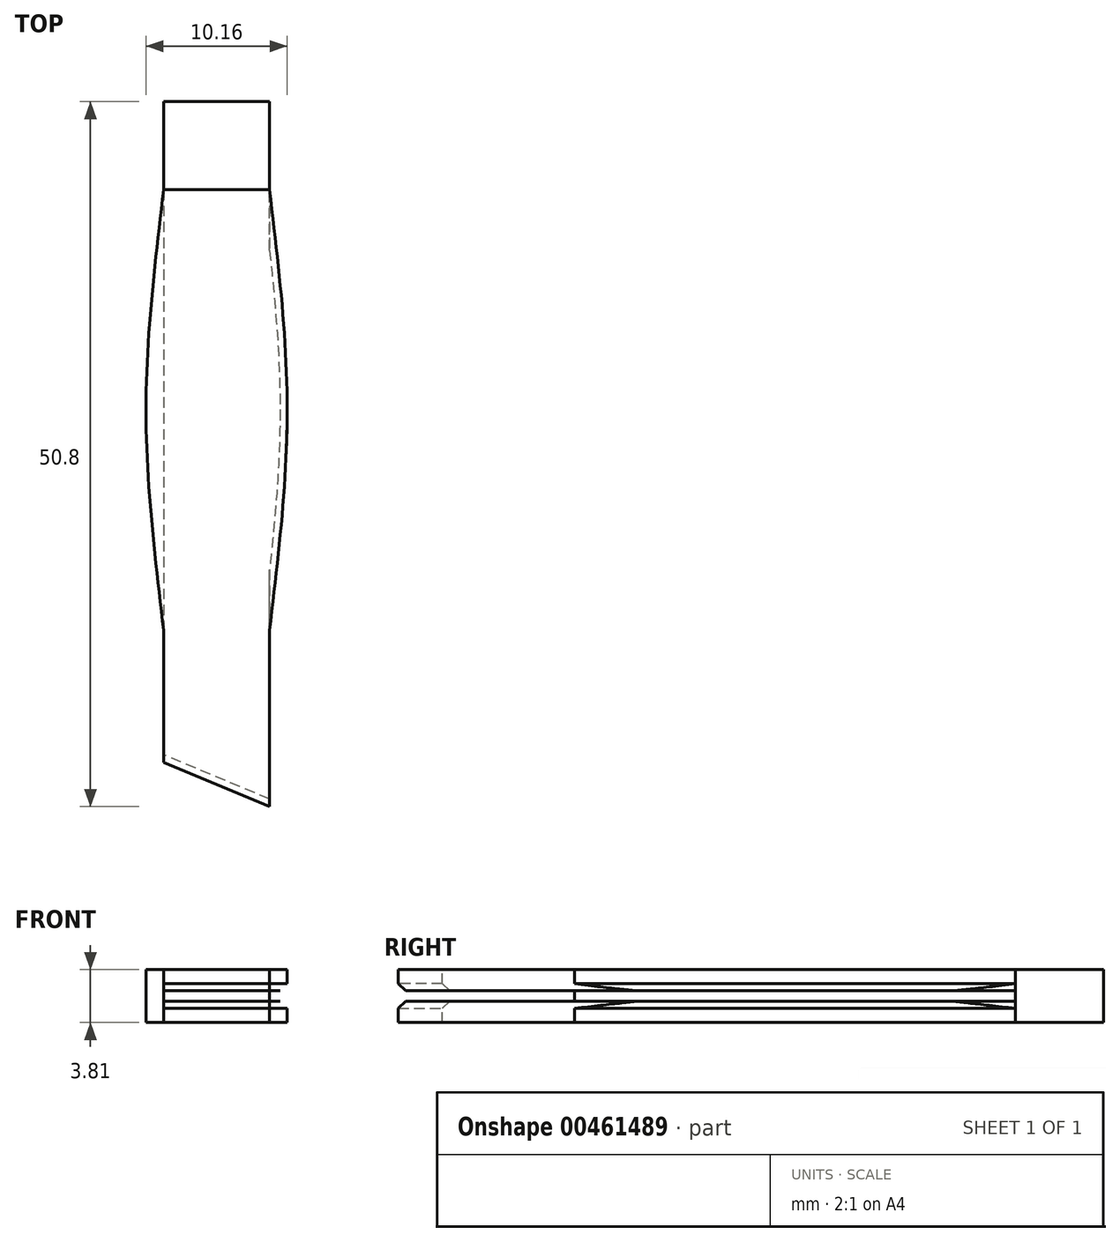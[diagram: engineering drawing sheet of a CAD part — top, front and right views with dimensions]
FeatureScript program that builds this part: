
annotation { "Feature Type Name" : "Feature", "Feature Type Description" : "" }
export const myFeature = defineFeature(function(context is Context, id is Id, definition is map)
    precondition{}
    {
        {
            var Q0;
            Q0=qCreatedBy(makeId("Front.planeOp"),FACE);
            var sketch = newSketch(context, id + "F0", { "sketchPlane" : qUnion([Q0])});
            skLineSegment(sketch, "E0.bottom", {"start": v(0, 0) * mm, "end": v(7.62, 0) * mm});
            skLineSegment(sketch, "E0.top", {"start": v(0, 3.81) * mm, "end": v(7.62, 3.81) * mm});
            skLineSegment(sketch, "E0.left", {"start": v(0, 0) * mm, "end": v(0, 3.81) * mm});
            skLineSegment(sketch, "E0.right", {"start": v(7.62, 0) * mm, "end": v(7.62, 3.81) * mm});
            skSolve(sketch);
        }
        {
            var Q0;
            Q0=makeQuery(id+"F0.imprint","IMPRINT",FACE,{"disambiguationData":[TD([[makeQuery(id+"F0.imprint","IMPRINT",EDGE,{"derivedFrom":sQuery(id+"F0.wireOp",EDGE,"E0.bottom")}),1.0]])]});
            extrude(context, id + "F1", {"entities" : qUnion([Q0]), "depth" : 6.35 * mm});
        }
        {
            var Q0;
            Q0=qCreatedBy(makeId("Top.planeOp"),FACE);
            var sketch = newSketch(context, id + "F2", { "sketchPlane" : qUnion([Q0])});
            skLineSegment(sketch, "E1.bottom", {"start": v(0, 0) * mm, "end": v(7.62, 0) * mm});
            skLineSegment(sketch, "E1.top", {"start": v(0, -6.35) * mm, "end": v(7.62, -6.35) * mm});
            skLineSegment(sketch, "E1.left", {"start": v(0, 0) * mm, "end": v(0, -6.35) * mm});
            skLineSegment(sketch, "E1.right", {"start": v(7.62, 0) * mm, "end": v(7.62, -6.35) * mm});
            skLineSegment(sketch, "E2", {"start": v(0, -6.35) * mm, "end": v(0, -12.7) * mm});
            skLineSegment(sketch, "E3", {"start": v(7.62, -6.35) * mm, "end": v(7.62, -12.7) * mm});
            skLineSegment(sketch, "E4", {"start": v(0, -44.45) * mm, "end": v(7.62, -44.45) * mm});
            skLineSegment(sketch, "E5.top", {"start": v(0, -57.15) * mm, "end": v(7.62, -57.15) * mm});
            skLineSegment(sketch, "E5.left", {"start": v(0, -44.45) * mm, "end": v(0, -57.15) * mm});
            skLineSegment(sketch, "E5.right", {"start": v(7.62, -44.45) * mm, "end": v(7.62, -57.15) * mm});
            skLineSegment(sketch, "E6", {"start": v(0, -12.7) * mm, "end": v(0, -44.45) * mm});
            skLineSegment(sketch, "E7", {"start": v(7.62, -12.7) * mm, "end": v(7.62, -44.45) * mm});
            skLineSegment(sketch, "E8", {"start": v(7.62, -28.58) * mm, "end": v(0, -28.58) * mm});
            skLineSegment(sketch, "E9", {"start": v(0, -28.58) * mm, "end": v(-1.27, -28.58) * mm});
            skLineSegment(sketch, "E10", {"start": v(7.62, -28.58) * mm, "end": v(8.9, -28.58) * mm});
            skFitSpline(sketch, "E11", {"points": [v(0, -12.7) * mm, v(-1.27, -28.58) * mm, v(0, -44.45) * mm], "startDerivative": vector(-3.81, -31.75) * mm, "endDerivative": vector(3.81, -31.75) * mm});
            skFitSpline(sketch, "E12", {"points": [v(7.62, -12.7) * mm, v(8.9, -28.58) * mm, v(7.62, -44.45) * mm], "startDerivative": vector(3.81, -31.75) * mm, "endDerivative": vector(-3.81, -31.75) * mm});
            skSolve(sketch);
        }
        {
            var Q0;
            Q0=makeQuery(id+"F2.imprint","IMPRINT",FACE,{"disambiguationData":[TD([[makeQuery(id+"F2.imprint","IMPRINT",EDGE,{"derivedFrom":sQuery(id+"F2.wireOp",EDGE,"E1.top")}),-1.0]])]});
            var Q1;
            Q1=makeQuery(id+"F2.imprint","IMPRINT",FACE,{"disambiguationData":[TD([[makeQuery(id+"F2.imprint","IMPRINT",EDGE,{"derivedFrom":sQuery(id+"F2.wireOp",EDGE,"E5.top")}),1.0]])]});
            var Q2;
            {var subQ3=sQuery(id+"F2.wireOp",EDGE,"E9");Q2=makeQuery(id+"F2.imprint","IMPRINT",FACE,{"disambiguationData":[TD([[makeQuery(id+"F2.imprint","IMPRINT",EDGE,{"derivedFrom":subQ3}),1.0]])]});}
            var Q3;
            {var subQ3=sQuery(id+"F2.wireOp",EDGE,"E9");Q3=makeQuery(id+"F2.imprint","IMPRINT",FACE,{"disambiguationData":[TD([[makeQuery(id+"F2.imprint","IMPRINT",EDGE,{"derivedFrom":subQ3}),-1.0]])]});}
            var Q4;
            {var subQ3=sQuery(id+"F2.wireOp",EDGE,"E8");Q4=makeQuery(id+"F2.imprint","IMPRINT",FACE,{"disambiguationData":[TD([[makeQuery(id+"F2.imprint","IMPRINT",EDGE,{"derivedFrom":subQ3}),1.0]])]});}
            var Q5;
            {var subQ3=sQuery(id+"F2.wireOp",EDGE,"E10");Q5=makeQuery(id+"F2.imprint","IMPRINT",FACE,{"disambiguationData":[TD([[makeQuery(id+"F2.imprint","IMPRINT",EDGE,{"derivedFrom":subQ3}),-1.0]])]});}
            var Q6;
            {var subQ3=sQuery(id+"F2.wireOp",EDGE,"E10");Q6=makeQuery(id+"F2.imprint","IMPRINT",FACE,{"disambiguationData":[TD([[makeQuery(id+"F2.imprint","IMPRINT",EDGE,{"derivedFrom":subQ3}),1.0]])]});}
            extrude(context, id + "F3", {"entities" : qUnion([Q0, Q1, Q2, Q3, Q4, Q5, Q6]), "operationType" : NewBodyOperationType.ADD, "depth" : 3.8 * mm});
        }
        {
            var Q0;
            Q0=makeQuery(id+"F3.opExtrude","SWEPT_FACE",FACE,{"disambiguationData":[OSD([sQuery(id+"F2.wireOp",EDGE,"E5.top")])]});
            var sketch = newSketch(context, id + "F4", { "sketchPlane" : qUnion([Q0])});
            skLineSegment(sketch, "E13", {"start": v(0, 3.81) * mm, "end": v(7.62, 3.81) * mm});
            skLineSegment(sketch, "E14.bottom", {"start": v(-4.88, 3.81) * mm, "end": v(12.52, 3.81) * mm});
            skLineSegment(sketch, "E14.top", {"start": v(-4.88, 0) * mm, "end": v(12.52, 0) * mm});
            skLineSegment(sketch, "E14.left", {"start": v(-4.88, 3.81) * mm, "end": v(-4.88, 0) * mm});
            skLineSegment(sketch, "E15", {"start": v(-4.88, 3.81) * mm, "end": v(-4.88, 2.29) * mm});
            skLineSegment(sketch, "E16", {"start": v(-4.88, 0) * mm, "end": v(-4.88, 1.52) * mm});
            skLineSegment(sketch, "E17", {"start": v(12.52, 0) * mm, "end": v(12.52, 1.52) * mm});
            skLineSegment(sketch, "E18.bottom", {"start": v(-4.88, 2.29) * mm, "end": v(12.52, 2.29) * mm});
            skLineSegment(sketch, "E18.top", {"start": v(-4.88, 1.52) * mm, "end": v(12.52, 1.52) * mm});
            skLineSegment(sketch, "E18.left", {"start": v(-4.88, 2.29) * mm, "end": v(-4.88, 1.52) * mm});
            skLineSegment(sketch, "E18.right", {"start": v(12.52, 2.29) * mm, "end": v(12.52, 1.52) * mm});
            skSolve(sketch);
        }
        {
            var Q0;
            {var subQ0=sQuery(id+"F4.wireOp",EDGE,"E18.bottom");var subQ1=sQuery(id+"F2.wireOp",EDGE,"E5.top");var subQ2=makeQuery(id+"F3.opExtrude","SWEPT_EDGE",EDGE,{"disambiguationData":[OSD([subQ1,sQuery(id+"F2.wireOp",EDGE,"E5.right")])]});var subQ3=makeQuery(id+"F4.imprint","INTERSECT",VERTEX,{"derivedFrom":[subQ2,subQ0]});Q0=makeQuery(id+"F4.imprint","IMPRINT",FACE,{"disambiguationData":[TD([[makeQuery(id+"F4.imprint","IMPRINT",EDGE,{"disambiguationData":[TD([[subQ3,1.0]])],"derivedFrom":subQ0}),-1.0]])]});}
            var Q1;
            {var subQ0=sQuery(id+"F4.wireOp",EDGE,"E18.left");Q1=makeQuery(id+"F4.imprint","IMPRINT",FACE,{"disambiguationData":[TD([[makeQuery(id+"F4.imprint","IMPRINT",EDGE,{"derivedFrom":subQ0}),1.0]])]});}
            var Q2;
            {var subQ0=sQuery(id+"F4.wireOp",EDGE,"E18.right");Q2=makeQuery(id+"F4.imprint","IMPRINT",FACE,{"disambiguationData":[TD([[makeQuery(id+"F4.imprint","IMPRINT",EDGE,{"derivedFrom":subQ0}),-1.0]])]});}
            extrude(context, id + "F5", {"entities" : qUnion([Q0, Q1, Q2]), "operationType" : NewBodyOperationType.REMOVE, "oppositeDirection" : true, "depth" : 50.8 * mm});
        }
        {
            var Q0;
            Q0=makeQuery(id+"F3.boolean.opBoolean","MERGE",FACE,{"derivedFrom":[makeQuery(id+"F1.opExtrude","SWEPT_FACE",FACE,{"disambiguationData":[OSD([sQuery(id+"F0.wireOp",EDGE,"E0.top")])]}),makeQuery(id+"F3.opExtrude","CAP_FACE",FACE,{"disambiguationData":[OSD([sQuery(id+"F2.wireOp",EDGE,"E1.top"),sQuery(id+"F2.wireOp",EDGE,"E2"),sQuery(id+"F2.wireOp",EDGE,"E3"),sQuery(id+"F2.wireOp",EDGE,"277f9b0c-e394-4d01-b2aa-9fb8e24fa29d"),sQuery(id+"F2.wireOp",EDGE,"5b10a53d-1cbc-4650-926f-43f652588418"),sQuery(id+"F2.wireOp",EDGE,"E4"),sQuery(id+"F2.wireOp",EDGE,"E5.top"),sQuery(id+"F2.wireOp",EDGE,"E5.left"),sQuery(id+"F2.wireOp",EDGE,"E5.right")])],"isStart":false})]});
            var sketch = newSketch(context, id + "F6", { "sketchPlane" : qUnion([Q0])});
            skLineSegment(sketch, "E19", {"start": v(0, -44.45) * mm, "end": v(7.62, -44.45) * mm});
            skLineSegment(sketch, "E20.top", {"start": v(0, -57.15) * mm, "end": v(7.62, -57.15) * mm});
            skLineSegment(sketch, "E20.left", {"start": v(0, -44.45) * mm, "end": v(0, -57.15) * mm});
            skLineSegment(sketch, "E20.right", {"start": v(7.62, -44.45) * mm, "end": v(7.62, -57.15) * mm});
            skLineSegment(sketch, "E21", {"start": v(7.62, -57.15) * mm, "end": v(0, -53.98) * mm});
            skSolve(sketch);
        }
        {
            var Q0;
            {var subQ0=sQuery(id+"F6.wireOp",EDGE,"E20.top");Q0=makeQuery(id+"F6.imprint","IMPRINT",FACE,{"disambiguationData":[TD([[makeQuery(id+"F6.imprint","IMPRINT",EDGE,{"derivedFrom":subQ0}),1.0]])]});}
            extrude(context, id + "F7", {"entities" : qUnion([Q0]), "operationType" : NewBodyOperationType.REMOVE, "oppositeDirection" : true, "depth" : 25.4 * mm});
        }
        {
            var Q0;
            Q0=makeQuery(id+"F7.boolean.opBoolean","INTERSECT",EDGE,{"derivedFrom":[makeQuery(id+"F5.boolean.opBoolean","COPY",FACE,{"derivedFrom":makeQuery(id+"F5.opExtrude","SWEPT_FACE",FACE,{"disambiguationData":[OSD([sQuery(id+"F4.wireOp",EDGE,"E18.bottom")])]})}),makeQuery(id+"F7.opExtrude","SWEPT_FACE",FACE,{"disambiguationData":[OSD([sQuery(id+"F6.wireOp",EDGE,"E21")])]})]});
            var Q1;
            Q1=makeQuery(id+"F7.boolean.opBoolean","INTERSECT",EDGE,{"derivedFrom":[makeQuery(id+"F5.boolean.opBoolean","COPY",FACE,{"derivedFrom":makeQuery(id+"F5.opExtrude","SWEPT_FACE",FACE,{"disambiguationData":[OSD([sQuery(id+"F4.wireOp",EDGE,"E18.top")])]})}),makeQuery(id+"F7.opExtrude","SWEPT_FACE",FACE,{"disambiguationData":[OSD([sQuery(id+"F6.wireOp",EDGE,"E21")])]})]});
            var Q2;
            Q2=makeQuery(id+"F5.boolean.opBoolean","INTERSECT",EDGE,{"derivedFrom":[makeQuery(id+"F3.opExtrude","SWEPT_FACE",FACE,{"disambiguationData":[OSD([sQuery(id+"F2.wireOp",EDGE,"E11")])]}),makeQuery(id+"F5.opExtrude","SWEPT_FACE",FACE,{"disambiguationData":[OSD([sQuery(id+"F4.wireOp",EDGE,"E18.bottom")])]})]});
            var Q3;
            Q3=makeQuery(id+"F5.boolean.opBoolean","INTERSECT",EDGE,{"derivedFrom":[makeQuery(id+"F3.opExtrude","SWEPT_FACE",FACE,{"disambiguationData":[OSD([sQuery(id+"F2.wireOp",EDGE,"E12")])]}),makeQuery(id+"F5.opExtrude","SWEPT_FACE",FACE,{"disambiguationData":[OSD([sQuery(id+"F4.wireOp",EDGE,"E18.bottom")])]})]});
            var Q4;
            Q4=makeQuery(id+"F5.boolean.opBoolean","INTERSECT",EDGE,{"derivedFrom":[makeQuery(id+"F3.opExtrude","SWEPT_FACE",FACE,{"disambiguationData":[OSD([sQuery(id+"F2.wireOp",EDGE,"E12")])]}),makeQuery(id+"F5.opExtrude","SWEPT_FACE",FACE,{"disambiguationData":[OSD([sQuery(id+"F4.wireOp",EDGE,"E18.top")])]})]});
            var Q5;
            Q5=makeQuery(id+"F5.boolean.opBoolean","INTERSECT",EDGE,{"derivedFrom":[makeQuery(id+"F3.opExtrude","SWEPT_FACE",FACE,{"disambiguationData":[OSD([sQuery(id+"F2.wireOp",EDGE,"E11")])]}),makeQuery(id+"F5.opExtrude","SWEPT_FACE",FACE,{"disambiguationData":[OSD([sQuery(id+"F4.wireOp",EDGE,"E18.top")])]})]});
            chamfer(context, id + "F8", {"entities" : qUnion([Q0, Q1, Q2, Q3, Q4, Q5]), "width" : 0.5 * mm, "tangentPropagation" : true});
        }
        {
            var Q0;
            Q0=makeQuery(id+"F3.boolean.opBoolean","MERGE",FACE,{"derivedFrom":[makeQuery(id+"F1.opExtrude","SWEPT_FACE",FACE,{"disambiguationData":[OSD([sQuery(id+"F0.wireOp",EDGE,"E0.top")])]}),makeQuery(id+"F3.opExtrude","CAP_FACE",FACE,{"disambiguationData":[OSD([sQuery(id+"F2.wireOp",EDGE,"E1.top"),sQuery(id+"F2.wireOp",EDGE,"E2"),sQuery(id+"F2.wireOp",EDGE,"E3"),sQuery(id+"F2.wireOp",EDGE,"E5.top"),sQuery(id+"F2.wireOp",EDGE,"E5.left"),sQuery(id+"F2.wireOp",EDGE,"E5.right"),sQuery(id+"F2.wireOp",EDGE,"E11"),sQuery(id+"F2.wireOp",EDGE,"E12")])],"isStart":false})]});
            var sketch = newSketch(context, id + "F9", { "sketchPlane" : qUnion([Q0])});
            skLineSegment(sketch, "E22.bottom", {"start": v(0, 0) * mm, "end": v(7.62, 0) * mm});
            skLineSegment(sketch, "E22.top", {"start": v(0, -12.7) * mm, "end": v(7.62, -12.7) * mm});
            skLineSegment(sketch, "E22.left", {"start": v(0, 0) * mm, "end": v(0, -12.7) * mm});
            skLineSegment(sketch, "E22.right", {"start": v(7.62, 0) * mm, "end": v(7.62, -12.7) * mm});
            skSolve(sketch);
        }
        {
            var Q0;
            Q0=makeQuery(id+"F9.imprint","IMPRINT",FACE,{"disambiguationData":[TD([[makeQuery(id+"F9.imprint","IMPRINT",EDGE,{"derivedFrom":sQuery(id+"F9.wireOp",EDGE,"E22.bottom")}),-1.0]])]});
            extrude(context, id + "F10", {"entities" : qUnion([Q0]), "operationType" : NewBodyOperationType.REMOVE, "oppositeDirection" : true, "depth" : 25.4 * mm});
        }
        {
            var Q0;
            Q0=makeQuery(id+"F3.boolean.opBoolean","MERGE",FACE,{"derivedFrom":[makeQuery(id+"F1.opExtrude","SWEPT_FACE",FACE,{"disambiguationData":[OSD([sQuery(id+"F0.wireOp",EDGE,"E0.top")])]}),makeQuery(id+"F3.opExtrude","CAP_FACE",FACE,{"disambiguationData":[OSD([sQuery(id+"F2.wireOp",EDGE,"E1.top"),sQuery(id+"F2.wireOp",EDGE,"E2"),sQuery(id+"F2.wireOp",EDGE,"E3"),sQuery(id+"F2.wireOp",EDGE,"E5.top"),sQuery(id+"F2.wireOp",EDGE,"E5.left"),sQuery(id+"F2.wireOp",EDGE,"E5.right"),sQuery(id+"F2.wireOp",EDGE,"E11"),sQuery(id+"F2.wireOp",EDGE,"E12")])],"isStart":false})]});
            var sketch = newSketch(context, id + "F11", { "sketchPlane" : qUnion([Q0])});
            skLineSegment(sketch, "E23.bottom", {"start": v(0, -12.7) * mm, "end": v(7.62, -12.7) * mm});
            skLineSegment(sketch, "E23.top", {"start": v(0, -6.35) * mm, "end": v(7.62, -6.35) * mm});
            skLineSegment(sketch, "E23.left", {"start": v(0, -12.7) * mm, "end": v(0, -6.35) * mm});
            skLineSegment(sketch, "E23.right", {"start": v(7.62, -12.7) * mm, "end": v(7.62, -6.35) * mm});
            skSolve(sketch);
        }
        {
            var Q0;
            Q0=makeQuery(id+"F11.imprint","IMPRINT",FACE,{"disambiguationData":[TD([[makeQuery(id+"F11.imprint","IMPRINT",EDGE,{"derivedFrom":sQuery(id+"F11.wireOp",EDGE,"E23.bottom")}),1.0]])]});
            extrude(context, id + "F12", {"entities" : qUnion([Q0]), "oppositeDirection" : true, "depth" : 3.8 * mm});
        }
    });
